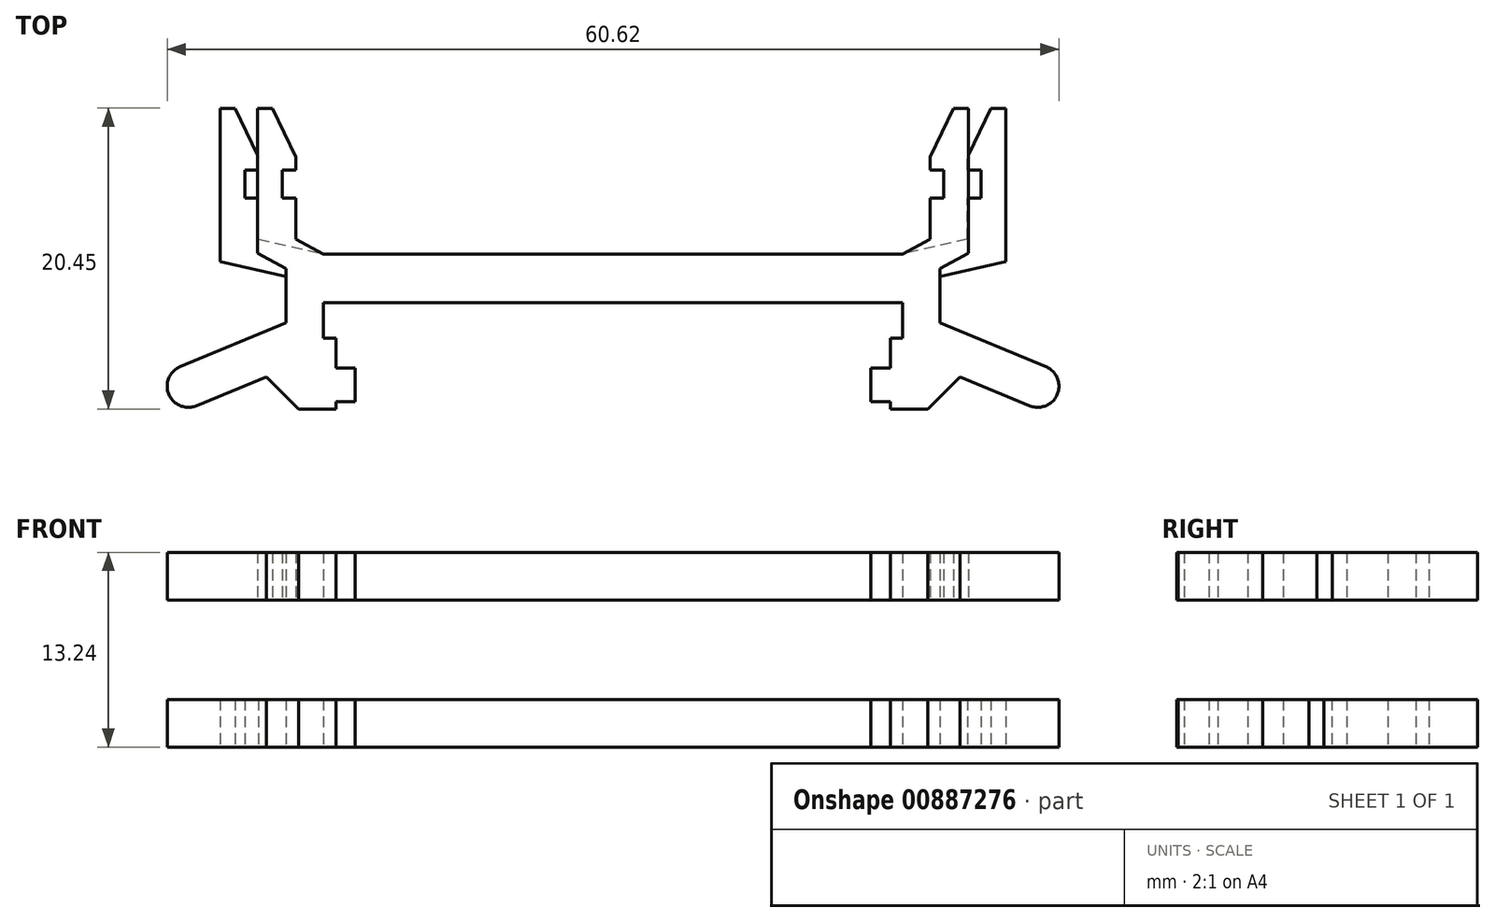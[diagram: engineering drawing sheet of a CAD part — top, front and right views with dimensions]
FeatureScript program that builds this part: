
annotation { "Feature Type Name" : "Feature", "Feature Type Description" : "" }
export const myFeature = defineFeature(function(context is Context, id is Id, definition is map)
    precondition{}
    {
        {
            var Q0;
            Q0=qCreatedBy(makeId("Top.planeOp"),FACE);
            var sketch = newSketch(context, id + "F0", { "sketchPlane" : qUnion([Q0])});
            skLineSegment(sketch, "E0.bottom", {"start": v(0, 1.65) * mm, "end": v(19.69, 1.65) * mm});
            skLineSegment(sketch, "E0.top", {"start": v(0, -1.65) * mm, "end": v(19.69, -1.65) * mm});
            skLineSegment(sketch, "E0.right", {"start": v(22.22, 0.1) * mm, "end": v(22.22, -1.65) * mm});
            skLineSegment(sketch, "E1", {"start": v(22.22, -1.65) * mm, "end": v(22.22, -3.04) * mm});
            skLineSegment(sketch, "E2", {"start": v(21.39, -8.89) * mm, "end": v(18.85, -8.89) * mm});
            skLineSegment(sketch, "E3", {"start": v(18.85, -8.89) * mm, "end": v(18.85, -8.38) * mm});
            skLineSegment(sketch, "E4", {"start": v(18.85, -8.38) * mm, "end": v(17.53, -8.38) * mm});
            skLineSegment(sketch, "E5", {"start": v(17.53, -8.38) * mm, "end": v(17.53, -6.1) * mm});
            skLineSegment(sketch, "E6", {"start": v(17.53, -6.1) * mm, "end": v(18.85, -6.1) * mm});
            skLineSegment(sketch, "E7", {"start": v(18.85, -6.1) * mm, "end": v(18.85, -4.06) * mm});
            skLineSegment(sketch, "E8", {"start": v(18.85, -4.06) * mm, "end": v(19.69, -4.06) * mm});
            skLineSegment(sketch, "E9", {"start": v(19.69, -4.06) * mm, "end": v(19.69, -1.65) * mm});
            skLineSegment(sketch, "E10", {"start": v(0, 1.65) * mm, "end": v(0, -1.65) * mm});
            skLineSegment(sketch, "E11", {"start": v(18.85, -6.1) * mm, "end": v(18.85, -8.38) * mm, "construction": true});
            skLineSegment(sketch, "E12", {"start": v(19.69, -4.06) * mm, "end": v(20.95, -4.06) * mm, "construction": true});
            skLineSegment(sketch, "E13", {"start": v(20.95, -4.06) * mm, "end": v(28.87, -7.34) * mm, "construction": true});
            skArc(sketch, "E14", {"start": v(28.33, -8.67) * mm, "mid": v(30.2, -7.9) * mm, "end": v(29.42, -6.02) * mm});
            skLineSegment(sketch, "E15", {"start": v(28.33, -8.67) * mm, "end": v(23.57, -6.7) * mm});
            skLineSegment(sketch, "E16", {"start": v(29.42, -6.02) * mm, "end": v(22.23, -3.04) * mm});
            skLineSegment(sketch, "E17", {"start": v(21.39, -8.89) * mm, "end": v(23.57, -6.7) * mm});
            skLineSegment(sketch, "E18", {"start": v(24.1, 2.67) * mm, "end": v(24.1, 5.46) * mm});
            skLineSegment(sketch, "E19", {"start": v(26.7, 2.67) * mm, "end": v(26.7, 11.56) * mm});
            skLineSegment(sketch, "E20", {"start": v(24.1, 7.37) * mm, "end": v(25.02, 7.37) * mm});
            skLineSegment(sketch, "E21", {"start": v(25.02, 7.37) * mm, "end": v(25.02, 5.46) * mm});
            skLineSegment(sketch, "E22", {"start": v(25.02, 5.46) * mm, "end": v(24.1, 5.46) * mm});
            skLineSegment(sketch, "E23.trimOffspring", {"start": v(24.1, 7.37) * mm, "end": v(24.1, 8.26) * mm});
            skLineSegment(sketch, "E24", {"start": v(24.1, 2.67) * mm, "end": v(19.69, 1.65) * mm});
            skLineSegment(sketch, "E25", {"start": v(26.7, 2.67) * mm, "end": v(26.7, 1.13) * mm});
            skLineSegment(sketch, "E26", {"start": v(26.7, 1.13) * mm, "end": v(22.23, 0.1) * mm});
            skPoint(sketch, "E27", {"position": v(22.23, 0.1) * mm});
            skLineSegment(sketch, "E28", {"start": v(26.7, 11.56) * mm, "end": v(25.68, 11.56) * mm});
            skLineSegment(sketch, "E29", {"start": v(25.68, 11.56) * mm, "end": v(24.1, 8.26) * mm});
            skSolve(sketch);
        }
        {
            var Q0;
            Q0=qCreatedBy(makeId("Top.planeOp"),FACE);
            cPlane(context, id + "F1", {"entities" : qUnion([Q0]), "cplaneType" : CPlaneType.OFFSET, "offset" : 10 * mm, "width" : 150 * mm, "height" : 150 * mm});
        }
        {
            var Q0;
            Q0=qCreatedBy(id+"F1.planeOp",FACE);
            var sketch = newSketch(context, id + "F2", { "sketchPlane" : qUnion([Q0])});
            skLineSegment(sketch, "E30.bottom", {"start": v(0, 1.65) * mm, "end": v(19.69, 1.65) * mm});
            skLineSegment(sketch, "E30.top", {"start": v(0, -1.65) * mm, "end": v(19.69, -1.65) * mm});
            skLineSegment(sketch, "E30.right", {"start": v(22.22, 0.66) * mm, "end": v(22.22, -1.65) * mm});
            skLineSegment(sketch, "E31", {"start": v(22.22, -1.65) * mm, "end": v(22.22, -3.04) * mm});
            skLineSegment(sketch, "E32", {"start": v(21.39, -8.89) * mm, "end": v(18.85, -8.89) * mm});
            skLineSegment(sketch, "E33", {"start": v(18.85, -8.89) * mm, "end": v(18.85, -8.38) * mm});
            skLineSegment(sketch, "E34", {"start": v(18.85, -8.38) * mm, "end": v(17.53, -8.38) * mm});
            skLineSegment(sketch, "E35", {"start": v(17.53, -8.38) * mm, "end": v(17.53, -6.1) * mm});
            skLineSegment(sketch, "E36", {"start": v(17.53, -6.1) * mm, "end": v(18.85, -6.1) * mm});
            skLineSegment(sketch, "E37", {"start": v(18.85, -6.1) * mm, "end": v(18.85, -4.06) * mm});
            skLineSegment(sketch, "E38", {"start": v(18.85, -4.06) * mm, "end": v(19.69, -4.06) * mm});
            skLineSegment(sketch, "E39", {"start": v(19.69, -4.06) * mm, "end": v(19.69, -1.65) * mm});
            skLineSegment(sketch, "E40", {"start": v(0, 1.65) * mm, "end": v(0, -1.65) * mm});
            skLineSegment(sketch, "E41", {"start": v(18.85, -6.1) * mm, "end": v(18.85, -8.38) * mm, "construction": true});
            skLineSegment(sketch, "E42", {"start": v(19.69, -4.06) * mm, "end": v(20.95, -4.06) * mm, "construction": true});
            skLineSegment(sketch, "E43", {"start": v(20.95, -4.06) * mm, "end": v(28.87, -7.34) * mm, "construction": true});
            skArc(sketch, "E44", {"start": v(28.33, -8.67) * mm, "mid": v(30.2, -7.9) * mm, "end": v(29.42, -6.02) * mm});
            skLineSegment(sketch, "E45", {"start": v(28.33, -8.67) * mm, "end": v(23.57, -6.7) * mm});
            skLineSegment(sketch, "E46", {"start": v(29.42, -6.02) * mm, "end": v(22.23, -3.04) * mm});
            skLineSegment(sketch, "E47", {"start": v(21.39, -8.89) * mm, "end": v(23.57, -6.7) * mm});
            skLineSegment(sketch, "E48", {"start": v(21.56, 2.67) * mm, "end": v(21.56, 5.46) * mm});
            skLineSegment(sketch, "E49", {"start": v(24.16, 2.67) * mm, "end": v(24.16, 11.56) * mm});
            skLineSegment(sketch, "E50", {"start": v(21.56, 7.37) * mm, "end": v(22.48, 7.37) * mm});
            skLineSegment(sketch, "E51", {"start": v(22.48, 7.37) * mm, "end": v(22.48, 5.46) * mm});
            skLineSegment(sketch, "E52", {"start": v(22.48, 5.46) * mm, "end": v(21.56, 5.46) * mm});
            skLineSegment(sketch, "E53.trimOffspring", {"start": v(21.56, 7.37) * mm, "end": v(21.56, 8.26) * mm});
            skLineSegment(sketch, "E54", {"start": v(21.56, 2.67) * mm, "end": v(19.69, 1.65) * mm});
            skLineSegment(sketch, "E55", {"start": v(24.16, 2.67) * mm, "end": v(24.16, 1.7) * mm});
            skLineSegment(sketch, "E56", {"start": v(24.16, 1.7) * mm, "end": v(22.23, 0.66) * mm});
            skPoint(sketch, "E57", {"position": v(22.23, 0.66) * mm});
            skLineSegment(sketch, "E58", {"start": v(24.16, 11.56) * mm, "end": v(23.14, 11.56) * mm});
            skLineSegment(sketch, "E59", {"start": v(23.14, 11.56) * mm, "end": v(21.56, 8.26) * mm});
            skSolve(sketch);
        }
        {
            var Q0;
            Q0=makeQuery(id+"F0.imprint","IMPRINT",FACE,{"disambiguationData":[TD([[makeQuery(id+"F0.imprint","IMPRINT",EDGE,{"derivedFrom":sQuery(id+"F0.wireOp",EDGE,"E0.bottom")}),-1.0]])]});
            var Q1;
            Q1=makeQuery(id+"F2.imprint","IMPRINT",FACE,{"disambiguationData":[TD([[makeQuery(id+"F2.imprint","IMPRINT",EDGE,{"derivedFrom":sQuery(id+"F2.wireOp",EDGE,"E30.bottom")}),-1.0]])]});
            extrude(context, id + "F3", {"entities" : qUnion([Q0, Q1]), "depth" : 3.24 * mm, "offsetDistance" : 25.4 * mm});
        }
        {
            var Q0;
            Q0=makeQuery(id+"F3.opExtrude","SWEPT_BODY",BODY,{"disambiguationData":[OSD([sQuery(id+"F0.wireOp",EDGE,"E0.bottom"),sQuery(id+"F0.wireOp",EDGE,"E0.top"),sQuery(id+"F0.wireOp",EDGE,"E0.right"),sQuery(id+"F0.wireOp",EDGE,"E1"),sQuery(id+"F0.wireOp",EDGE,"E2"),sQuery(id+"F0.wireOp",EDGE,"E3"),sQuery(id+"F0.wireOp",EDGE,"E4"),sQuery(id+"F0.wireOp",EDGE,"E5"),sQuery(id+"F0.wireOp",EDGE,"E6"),sQuery(id+"F0.wireOp",EDGE,"E7"),sQuery(id+"F0.wireOp",EDGE,"E8"),sQuery(id+"F0.wireOp",EDGE,"E9"),sQuery(id+"F0.wireOp",EDGE,"E10"),sQuery(id+"F0.wireOp",EDGE,"E14"),sQuery(id+"F0.wireOp",EDGE,"E15"),sQuery(id+"F0.wireOp",EDGE,"E16"),sQuery(id+"F0.wireOp",EDGE,"E17"),sQuery(id+"F0.wireOp",EDGE,"E18"),sQuery(id+"F0.wireOp",EDGE,"E19"),sQuery(id+"F0.wireOp",EDGE,"7mUs4iZy-VCOA-Ia98-5NlY-xLhZukfP8Rcz"),sQuery(id+"F0.wireOp",EDGE,"E20"),sQuery(id+"F0.wireOp",EDGE,"E21"),sQuery(id+"F0.wireOp",EDGE,"E22"),sQuery(id+"F0.wireOp",EDGE,"E23.trimOffspring"),sQuery(id+"F0.wireOp",EDGE,"E24"),sQuery(id+"F0.wireOp",EDGE,"E25"),sQuery(id+"F0.wireOp",EDGE,"E26")])]});
            var Q1;
            Q1=makeQuery(id+"F3.opExtrude","SWEPT_BODY",BODY,{"disambiguationData":[OSD([sQuery(id+"F2.wireOp",EDGE,"E30.bottom"),sQuery(id+"F2.wireOp",EDGE,"E30.top"),sQuery(id+"F2.wireOp",EDGE,"E30.right"),sQuery(id+"F2.wireOp",EDGE,"E31"),sQuery(id+"F2.wireOp",EDGE,"E32"),sQuery(id+"F2.wireOp",EDGE,"E33"),sQuery(id+"F2.wireOp",EDGE,"E34"),sQuery(id+"F2.wireOp",EDGE,"E35"),sQuery(id+"F2.wireOp",EDGE,"E36"),sQuery(id+"F2.wireOp",EDGE,"E37"),sQuery(id+"F2.wireOp",EDGE,"E38"),sQuery(id+"F2.wireOp",EDGE,"E39"),sQuery(id+"F2.wireOp",EDGE,"E40"),sQuery(id+"F2.wireOp",EDGE,"E44"),sQuery(id+"F2.wireOp",EDGE,"E45"),sQuery(id+"F2.wireOp",EDGE,"E46"),sQuery(id+"F2.wireOp",EDGE,"E47"),sQuery(id+"F2.wireOp",EDGE,"E48"),sQuery(id+"F2.wireOp",EDGE,"E49"),sQuery(id+"F2.wireOp",EDGE,"E50"),sQuery(id+"F2.wireOp",EDGE,"E51"),sQuery(id+"F2.wireOp",EDGE,"E52"),sQuery(id+"F2.wireOp",EDGE,"E53.trimOffspring"),sQuery(id+"F2.wireOp",EDGE,"E54"),sQuery(id+"F2.wireOp",EDGE,"E55"),sQuery(id+"F2.wireOp",EDGE,"E56"),sQuery(id+"F2.wireOp",EDGE,"E58"),sQuery(id+"F2.wireOp",EDGE,"E59")])]});
            var Q2;
            Q2=qCreatedBy(makeId("Right.planeOp"),FACE);
            mirror(context, id + "F4", {"operationType" : NewBodyOperationType.ADD, "entities" : qUnion([Q0, Q1]), "mirrorPlane" : qUnion([Q2])});
        }
    });
